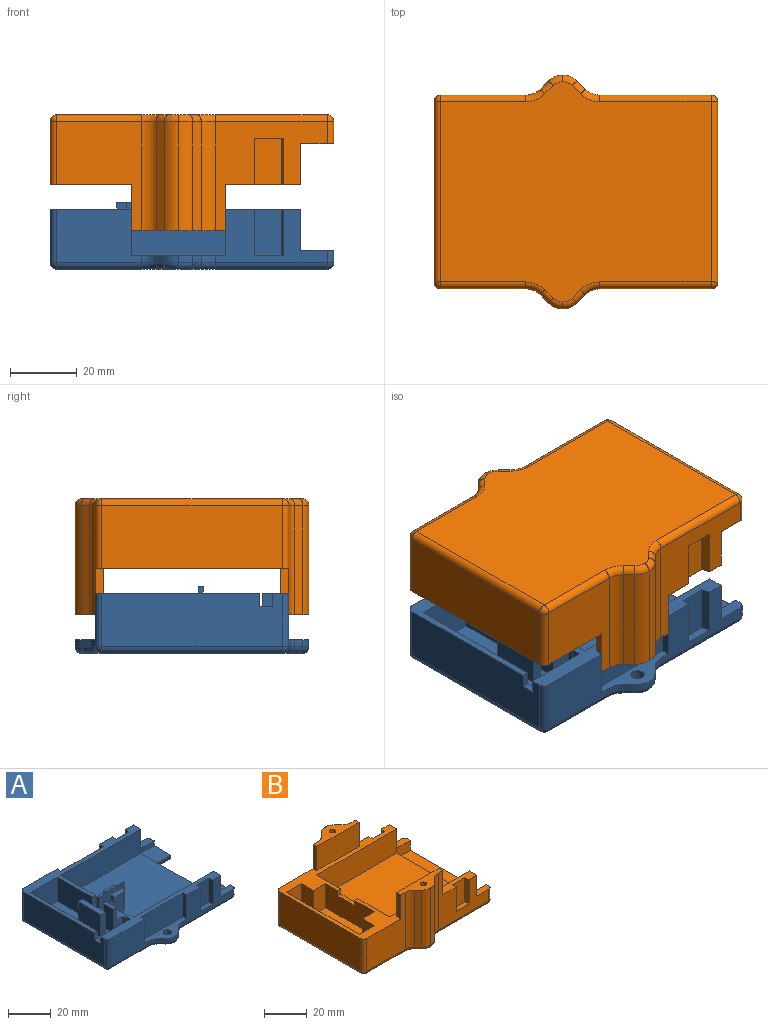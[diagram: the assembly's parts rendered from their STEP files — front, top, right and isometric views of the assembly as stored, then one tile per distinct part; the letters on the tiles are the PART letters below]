
ASSEMBLY  parts=2 mates=1
PART A: 140 faces, bbox 85x70x20 mm
  f0: plane 75x7.93mm, normal (0,0,1), area 280mm2, adj f3,f4,f9,f22,f23,f45,f46,f47
  f1: plane 48.25x13.88mm, normal (1,0,0), area 653.5mm2, adj f8,f51,f53,f54,f138,f139
  f2: plane 53x48.25mm, normal (0,0,1), area 2356.1mm2, adj f3,f7,f10,f11,f12,f13,f33,f34
  f3: plane 53x13.88mm, normal (0,1,0), area 694.8mm2, adj f0,f2,f9,f71,f72,f85
  f4: plane 33.51x15.88mm, normal (0,-1,0), area 272.1mm2, adj f0,f17,f19,f47,f48,f50,f83,f85
  f5: plane 12.88x3.65mm, normal (1,0,0), area 16.5mm2, adj f77,f78,f83,f84,f102,f103
  f6: plane 33.51x15.88mm, normal (0,1,0), area 272.1mm2, adj f8,f18,f20,f39,f41,f42,f82,f85
  f7: plane 53x13.88mm, normal (0,-1,0), area 735.4mm2, adj f2,f8,f13,f85
  f8: plane 75x49.13mm, normal (0,0,1), area 408mm2, adj f1,f6,f7,f13,f21,f22,f39,f40
  f9: plane 6.88x3.05mm, normal (1,0,0), area 21mm2, adj f0,f3,f72,f74
  f10: plane 13.88x11.3mm, normal (0,-1,0), area 89.3mm2, adj f2,f16,f32,f33,f63,f64,f71,f72
  f11: plane 13.88x0.8mm, normal (1,0,0), area 7.7mm2, adj f2,f16,f33,f34,f60,f64
  f12: plane 13.88x0.8mm, normal (1,0,0), area 7.7mm2, adj f2,f14,f36,f37,f65,f70
  f13: plane 23x13.88mm, normal (1,0,0), area 317.9mm2, adj f2,f7,f8,f38,f67,f70
  f14: plane 8.5x2.88mm, normal (0,0,1), area 20.8mm2, adj f12,f37,f38,f65,f66
  f15: plane 6.7x2mm, normal (0,0,1), area 13.4mm2, adj f32,f52,f59,f73
  f16: plane 8.5x2.88mm, normal (0,0,1), area 20.8mm2, adj f10,f11,f33,f60,f63
  f17: plane 8.67x2.5mm, normal (0,0,1), area 20.8mm2, adj f4,f48,f49,f50
  f18: plane 28x8.5mm, normal (0,0,1), area 123.4mm2, adj f6,f21,f28,f29,f30,f42,f43,f44
  f19: plane 28x8.5mm, normal (0,0,1), area 123.4mm2, adj f4,f23,f24,f25,f26,f45,f46,f47
  f20: plane 8.67x2.5mm, normal (0,0,1), area 20.8mm2, adj f6,f39,f40,f41
  f21: plane 25.51x15.88mm, normal (0,1,0), area 363.2mm2, adj f8,f18,f44,f94,f132,f137
  f22: plane 54x15.88mm, normal (-1,0,0), area 841.3mm2, adj f0,f8,f53,f127,f132,f133,f138,f139
  f23: plane 25.51x15.88mm, normal (0,-1,0), area 363.2mm2, adj f0,f19,f45,f87,f127,f128
  f24: plane 2.49x2.49mm, normal (-0.71,-0.71,0), area 7mm2, adj f19,f87,f88,f121,f123
  f25: plane 2.1x0.03mm, normal (0,-1,0), area 0.1mm2, adj f19,f88,f89,f117
  f26: plane 2.49x2.49mm, normal (0.71,-0.71,0), area 7mm2, adj f19,f89,f90,f110,f113
  f27: plane 12.88x3.65mm, normal (1,0,0), area 16.5mm2, adj f79,f80,f81,f82,f111,f112
  f28: plane 2.49x2.49mm, normal (0.71,0.71,0), area 7mm2, adj f18,f91,f92,f120,f122
  f29: plane 2.1x0.03mm, normal (0,1,0), area 0.1mm2, adj f18,f92,f93,f126
  f30: plane 2.49x2.49mm, normal (-0.71,0.71,0), area 7mm2, adj f18,f93,f94,f131,f134
  f31: plane 81x62.84mm, normal (0,0,-1), area 4097.4mm2, adj f57,f58,f103,f105,f106,f107,f108,f109
  f32: plane 6.88x6.7mm, normal (1,0,0), area 46.1mm2, adj f10,f15,f59,f72,f73
  f33: plane 13.88x2.7mm, normal (0.71,-0.71,0), area 53mm2, adj f2,f10,f11,f16
  f34: plane 15.88x14mm, normal (0,-1,0), area 111.8mm2, adj f2,f11,f35,f61,f64,f86
  f35: plane 15.88x0.5mm, normal (1,0,0), area 7.9mm2, adj f2,f34,f36,f86
  f36: plane 15.88x14mm, normal (0,1,0), area 111.7mm2, adj f2,f12,f35,f69,f70,f86
  f37: plane 13.88x2.7mm, normal (0.71,0.71,0), area 53mm2, adj f2,f12,f14,f38
  f38: plane 13.88x11.3mm, normal (0,1,0), area 129.9mm2, adj f2,f13,f14,f37,f66,f70,f101
  f39: plane 13.88x2.5mm, normal (-0.97,0.26,0), area 35.9mm2, adj f6,f8,f20,f40
  f40: plane 13.88x8mm, normal (0,1,0), area 111mm2, adj f8,f20,f39,f41
  f41: plane 13.88x2.5mm, normal (1,0,0), area 34.7mm2, adj f6,f8,f20,f40
  f42: plane 13.88x2.5mm, normal (-1,0,0), area 34.7mm2, adj f6,f8,f18,f43
  f43: plane 28x13.88mm, normal (0,1,0), area 388.5mm2, adj f8,f18,f42,f44
  f44: plane 13.88x2.5mm, normal (1,0,0), area 34.7mm2, adj f8,f18,f21,f43
  f45: plane 13.88x2.5mm, normal (1,0,0), area 34.7mm2, adj f0,f19,f23,f46
  f46: plane 28x13.88mm, normal (0,-1,0), area 388.5mm2, adj f0,f19,f45,f47
  f47: plane 13.88x2.5mm, normal (-1,0,0), area 34.7mm2, adj f0,f4,f19,f46
  f48: plane 13.88x2.5mm, normal (1,0,0), area 34.7mm2, adj f0,f4,f17,f49
  f49: plane 13.88x8mm, normal (0,-1,0), area 111mm2, adj f0,f17,f48,f50
  f50: plane 13.88x2.5mm, normal (-0.97,-0.26,0), area 35.9mm2, adj f0,f4,f17,f49
  f51: plane 18x13.88mm, normal (0,-1,0), area 249.8mm2, adj f1,f8,f52,f54
  f52: plane 48.25x15.88mm, normal (-1,0,0), area 536mm2, adj f0,f8,f15,f51,f53,f54,f59,f62
  f53: plane 20x13.88mm, normal (0,1,0), area 257.8mm2, adj f0,f1,f22,f52,f54,f139
  f54: plane 48.25x18mm, normal (0,0,1), area 823.5mm2, adj f1,f51,f52,f53,f95,f96,f97,f98
  f55: cylinder r=2mm len=4mm, axis (0,0,-1), area 31.4mm2, adj f18,f57
  f56: cylinder r=2mm len=4mm, axis (0,0,-1), area 31.4mm2, adj f19,f58
  f57: cone r=2mm half-angle=45deg, axis (0,0,-1), area 36.7mm2, adj f31,f55,f122,f124,f126,f129,f131
  f58: cone r=2mm half-angle=45deg, axis (0,0,-1), area 36.7mm2, adj f31,f56,f113,f115,f117,f119,f121
  f59: plane 5.38x2mm, normal (0,1,0), area 10.8mm2, adj f15,f32,f52,f64
  f60: plane 12x5.38mm, normal (0,1,0), area 48.3mm2, adj f11,f16,f63,f64,f100
  f61: plane 7.38x0.5mm, normal (1,0,0), area 3.7mm2, adj f34,f62,f64,f86
  f62: plane 7.38x3mm, normal (0,-1,0), area 22.1mm2, adj f52,f61,f64,f86
  f63: plane 2.88x1.88mm, normal (-1,0,0), area 5.4mm2, adj f10,f16,f60,f100
  f64: plane 16x3.5mm, normal (0,0,1), area 20mm2, adj f10,f11,f34,f52,f59,f60,f61,f62
  f65: plane 12x5.38mm, normal (0,-1,0), area 48.3mm2, adj f12,f14,f66,f70,f101
  f66: plane 2.88x1.88mm, normal (-1,0,0), area 5.4mm2, adj f14,f38,f65,f101
  f67: plane 5.38x2mm, normal (0,-1,0), area 10.8mm2, adj f8,f13,f52,f70
  f68: plane 7.38x3mm, normal (0,1,0), area 22.1mm2, adj f52,f69,f70,f86
  f69: plane 7.38x0.5mm, normal (1,0,0), area 3.7mm2, adj f36,f68,f70,f86
  f70: plane 16x3.73mm, normal (0,0,1), area 20.5mm2, adj f12,f13,f36,f38,f52,f65,f67,f68
  f71: plane 17.75x7mm, normal (1,0,0), area 124.3mm2, adj f2,f3,f10,f72
  f72: plane 17.75x5.8mm, normal (0,0,1), area 70.6mm2, adj f3,f9,f10,f32,f71,f73,f74,f75
  f73: plane 12.88x6.05mm, normal (0,-1,0), area 50mm2, adj f15,f32,f52,f72,f75,f76
  f74: plane 12.88x6.05mm, normal (0,1,0), area 50mm2, adj f0,f9,f52,f72,f75,f76
  f75: plane 8x6mm, normal (-1,0,0), area 48mm2, adj f72,f73,f74,f76
  f76: plane 8x6.05mm, normal (0,0,1), area 48.4mm2, adj f52,f73,f74,f75
  f77: plane 11.1x10mm, normal (0,0,1), area 111mm2, adj f5,f78,f84,f85
  f78: plane 10x0.9mm, normal (0,1,0), area 9mm2, adj f5,f77,f85,f105
  f79: plane 10x0.9mm, normal (0,-1,0), area 9mm2, adj f27,f80,f85,f109
  f80: plane 11.1x10mm, normal (0,0,1), area 111mm2, adj f27,f79,f81,f85
  f81: plane 10x2.75mm, normal (0,-1,0), area 27.5mm2, adj f27,f80,f82,f85
  f82: plane 10x3.78mm, normal (0,0,1), area 36.9mm2, adj f6,f27,f81,f85,f112
  f83: plane 10x3.78mm, normal (0,0,1), area 36.9mm2, adj f4,f5,f84,f85,f102
  f84: plane 10x2.75mm, normal (0,1,0), area 27.5mm2, adj f5,f77,f83,f85
  f85: plane 58x15.88mm, normal (1,0,0), area 203.7mm2, adj f0,f2,f3,f4,f6,f7,f8,f77
  f86: plane 17x1.5mm, normal (0,0,1), area 11.5mm2, adj f34,f35,f36,f52,f61,f62,f68,f69
  f87: cylinder r=6mm len=4.24mm, axis (0,0,1), area 9.4mm2, adj f19,f23,f24,f125
  f88: cylinder r=6mm len=4.24mm, axis (0,0,-1), area 9.7mm2, adj f19,f24,f25,f119
  f89: cylinder r=6mm len=4.24mm, axis (0,0,-1), area 9.7mm2, adj f19,f25,f26,f115
  f90: cylinder r=6mm len=4.24mm, axis (0,0,1), area 9.4mm2, adj f4,f19,f26,f108
  f91: cylinder r=6mm len=4.24mm, axis (0,0,1), area 9.4mm2, adj f6,f18,f28,f118
  f92: cylinder r=6mm len=4.24mm, axis (0,0,-1), area 9.7mm2, adj f18,f28,f29,f124
  f93: cylinder r=6mm len=4.24mm, axis (0,0,-1), area 9.7mm2, adj f18,f29,f30,f129
  f94: cylinder r=6mm len=4.24mm, axis (0,0,1), area 9.4mm2, adj f18,f21,f30,f136
  f95: plane 13x3mm, normal (0,1,0), area 39mm2, adj f54,f96,f98,f99
  f96: plane 15x13mm, normal (-1,0,0), area 195mm2, adj f54,f95,f97,f99
  f97: plane 13x3mm, normal (0,-1,0), area 39mm2, adj f54,f96,f98,f99
  f98: plane 15x13mm, normal (1,0,0), area 195mm2, adj f54,f95,f97,f99
  f99: plane 15x3mm, normal (0,0,1), area 45mm2, adj f95,f96,f97,f98
  f100: cylinder r=3.5mm len=3.5mm, axis (0,1,0), area 15.8mm2, adj f10,f60,f63,f64
  f101: cylinder r=3.5mm len=3.5mm, axis (0,1,0), area 15.8mm2, adj f38,f65,f66,f70
  f102: cylinder r=2mm len=3.65mm, axis (0,0,1), area 11.5mm2, adj f4,f5,f83,f104
  f103: cylinder r=2mm len=12.88mm, axis (0,1,0), area 38.2mm2, adj f5,f31,f104,f105
  f104: sphere r=2mm, area 6.3mm2, adj f102,f103,f106
  f105: cylinder r=2mm len=12mm, axis (1,0,0), area 31.4mm2, adj f31,f78,f103,f107
  f106: cylinder r=2mm len=33.51mm, axis (1,0,0), area 105.3mm2, adj f4,f31,f104,f108
  f107: cylinder r=2mm len=32.25mm, axis (0,1,0), area 93.3mm2, adj f31,f85,f105,f109
  f108: torus R=8mm, axis (0,0,1), area 16.6mm2, adj f31,f90,f106,f110
  f109: cylinder r=2mm len=12mm, axis (1,0,0), area 31.4mm2, adj f31,f79,f107,f111
  f110: cylinder r=2mm len=3.49mm, axis (0.71,0.71,0), area 9.2mm2, adj f26,f31,f108,f113
  f111: cylinder r=2mm len=12.88mm, axis (0,1,0), area 38.2mm2, adj f27,f31,f109,f114
  f112: cylinder r=2mm len=3.65mm, axis (0,0,-1), area 11.5mm2, adj f6,f27,f82,f114
  f113: bspline ~2.27x2.17mm, area 1.7mm2, adj f26,f58,f110,f115
  f114: sphere r=2mm, area 6.3mm2, adj f111,f112,f116
  f115: bspline ~6.14x3.55mm, area 11.5mm2, adj f58,f89,f113,f117
  f116: cylinder r=2mm len=33.51mm, axis (-1,0,0), area 105.3mm2, adj f6,f31,f114,f118
  f117: bspline ~1.91x1.4mm, area 0.1mm2, adj f25,f58,f115,f119
  f118: torus R=8mm, axis (0,0,1), area 16.6mm2, adj f31,f91,f116,f120
  f119: bspline ~5.92x3.89mm, area 11.5mm2, adj f58,f88,f117,f121
  f120: cylinder r=2mm len=3.49mm, axis (-0.71,0.71,0), area 9.2mm2, adj f28,f31,f118,f122
  f121: bspline ~2.27x2.17mm, area 1.7mm2, adj f24,f58,f119,f123
  f122: bspline ~2.27x2.17mm, area 1.7mm2, adj f28,f57,f120,f124
  f123: cylinder r=2mm len=3.49mm, axis (0.71,-0.71,0), area 9.2mm2, adj f24,f31,f121,f125
  f124: bspline ~5.92x3.89mm, area 11.5mm2, adj f57,f92,f122,f126
  f125: torus R=8mm, axis (0,0,1), area 16.6mm2, adj f31,f87,f123,f128
  f126: bspline ~1.91x1.4mm, area 0.1mm2, adj f29,f57,f124,f129
  f127: cylinder r=2mm len=15.88mm, axis (0,0,-1), area 49.9mm2, adj f0,f22,f23,f130
  f128: cylinder r=2mm len=25.51mm, axis (1,0,0), area 80.2mm2, adj f23,f31,f125,f130
  f129: bspline ~6.14x3.55mm, area 11.5mm2, adj f57,f93,f126,f131
  f130: sphere r=2mm, area 6.3mm2, adj f127,f128,f133
  f131: bspline ~2.27x2.17mm, area 1.7mm2, adj f30,f57,f129,f134
  f132: cylinder r=2mm len=15.88mm, axis (0,0,1), area 49.9mm2, adj f8,f21,f22,f135
  f133: cylinder r=2mm len=54mm, axis (0,-1,0), area 169.6mm2, adj f22,f31,f130,f135
  f134: cylinder r=2mm len=3.49mm, axis (-0.71,-0.71,0), area 9.2mm2, adj f30,f31,f131,f136
  f135: sphere r=2mm, area 6.3mm2, adj f132,f133,f137
  f136: torus R=8mm, axis (0,0,1), area 16.6mm2, adj f31,f94,f134,f137
  f137: cylinder r=2mm len=25.51mm, axis (-1,0,0), area 80.2mm2, adj f21,f31,f135,f136
  f138: plane 4x2mm, normal (0,-1,0), area 8mm2, adj f1,f8,f22,f139
  f139: plane 4x2mm, normal (0,0,1), area 8mm2, adj f1,f22,f53,f138
PART B: 92 faces, bbox 85x71x34.8 mm
  f0: plane 75x58mm, normal (0,0,1), area 846.4mm2, adj f1,f2,f4,f5,f6,f7,f12,f13
  f1: plane 48.25x13.88mm, normal (1,0,0), area 635.7mm2, adj f0,f3,f6,f7,f51,f52,f53
  f2: plane 32.25x13.88mm, normal (-1,0,0), area 413.7mm2, adj f0,f28,f29,f33,f51,f52,f53
  f3: plane 53x48.25mm, normal (0,0,1), area 2557.3mm2, adj f1,f6,f7,f48
  f4: plane 33.51x32.75mm, normal (0,-1,0), area 456.3mm2, adj f0,f8,f20,f22,f38,f41,f48,f50
  f5: plane 33.51x32.75mm, normal (0,1,0), area 456.3mm2, adj f0,f9,f23,f25,f36,f37,f48,f49
  f6: plane 53x13.88mm, normal (0,1,0), area 735.4mm2, adj f0,f1,f3,f48
  f7: plane 53x13.88mm, normal (0,-1,0), area 735.4mm2, adj f0,f1,f3,f48
  f8: plane 8.67x2.5mm, normal (0,0,1), area 20.8mm2, adj f4,f20,f21,f22
  f9: plane 8.67x2.5mm, normal (0,0,1), area 20.8mm2, adj f5,f23,f24,f25
  f10: plane 32.75x0.03mm, normal (0,1,0), area 1mm2, adj f37,f54,f61,f73
  f11: plane 32.75x2.49mm, normal (-0.71,0.71,0), area 115.1mm2, adj f37,f54,f55,f77
  f12: plane 32.75x25.51mm, normal (0,1,0), area 523.4mm2, adj f0,f34,f37,f55,f81,f82
  f13: plane 54x18.88mm, normal (-1,0,0), area 1019.3mm2, adj f0,f82,f86,f87
  f14: plane 32.75x25.51mm, normal (0,-1,0), area 523.4mm2, adj f0,f40,f41,f56,f87,f91
  f15: plane 32.75x2.49mm, normal (-0.71,-0.71,0), area 115.1mm2, adj f41,f56,f57,f88
  f16: plane 32.75x0.03mm, normal (0,-1,0), area 1mm2, adj f41,f57,f58,f83
  f17: plane 32.75x2.49mm, normal (0.71,-0.71,0), area 115.1mm2, adj f41,f58,f59,f78
  f18: plane 54x6.65mm, normal (1,0,0), area 74.1mm2, adj f46,f47,f49,f50,f63,f64,f69,f70
  f19: plane 32.75x2.49mm, normal (0.71,0.71,0), area 115.1mm2, adj f37,f60,f61,f68
  f20: plane 13.88x2.5mm, normal (1,0,0), area 34.7mm2, adj f0,f4,f8,f21
  f21: plane 13.88x8mm, normal (0,-1,0), area 111mm2, adj f0,f8,f20,f22
  f22: plane 13.88x2.5mm, normal (-0.97,-0.26,0), area 35.9mm2, adj f0,f4,f8,f21
  f23: plane 13.88x2.5mm, normal (-0.97,0.26,0), area 35.9mm2, adj f0,f5,f9,f24
  f24: plane 13.88x8mm, normal (0,1,0), area 111mm2, adj f0,f9,f23,f25
  f25: plane 13.88x2.5mm, normal (1,0,0), area 34.7mm2, adj f0,f5,f9,f24
  f26: plane 13.88x10mm, normal (0,-1,0), area 138.8mm2, adj f0,f27,f32,f33
  f27: plane 13.88x8mm, normal (-1,0,0), area 111mm2, adj f0,f26,f28,f33
  f28: plane 13.88x8mm, normal (0,-1,0), area 111mm2, adj f0,f2,f27,f33
  f29: plane 13.88x8mm, normal (0,1,0), area 111mm2, adj f0,f2,f30,f33
  f30: plane 13.88x8mm, normal (-1,0,0), area 111mm2, adj f0,f29,f31,f33
  f31: plane 13.88x10mm, normal (0,1,0), area 138.8mm2, adj f0,f30,f32,f33
  f32: plane 48.25x13.88mm, normal (1,0,0), area 669.5mm2, adj f0,f26,f31,f33
  f33: plane 48.25x18mm, normal (0,0,1), area 740.5mm2, adj f2,f26,f27,f28,f29,f30,f31,f32
  f34: plane 13.88x2.5mm, normal (-1,0,0), area 34.7mm2, adj f0,f12,f35,f37
  f35: plane 28x13.88mm, normal (0,-1,0), area 388.5mm2, adj f0,f34,f36,f37
  f36: plane 13.88x2.5mm, normal (1,0,0), area 34.7mm2, adj f0,f5,f35,f37
  f37: plane 28x8.5mm, normal (0,0,1), area 130.1mm2, adj f5,f10,f11,f12,f19,f34,f35,f36
  f38: plane 13.88x2.5mm, normal (1,0,0), area 34.7mm2, adj f0,f4,f39,f41
  f39: plane 28x13.88mm, normal (0,1,0), area 388.5mm2, adj f0,f38,f40,f41
  f40: plane 13.88x2.5mm, normal (-1,0,0), area 34.7mm2, adj f0,f14,f39,f41
  f41: plane 28x8.5mm, normal (0,0,1), area 130.1mm2, adj f4,f14,f15,f16,f17,f38,f39,f40
  f42: cylinder r=1.38mm len=10mm, axis (0,0,1), area 86.4mm2, adj f41,f43
  f43: plane 2.75x2.75mm, normal (0,0,1), area 5.9mm2, adj f42
  f44: cylinder r=1.38mm len=10mm, axis (0,0,1), area 86.4mm2, adj f37,f45
  f45: plane 2.75x2.75mm, normal (0,0,1), area 5.9mm2, adj f44
  f46: plane 10x5.65mm, normal (0,-1,0), area 56.5mm2, adj f18,f48,f49,f63
  f47: plane 10x5.65mm, normal (0,1,0), area 56.5mm2, adj f18,f48,f50,f63
  f48: plane 58x17.88mm, normal (1,0,0), area 324.6mm2, adj f0,f3,f4,f5,f6,f7,f46,f47
  f49: plane 10x3.78mm, normal (0,0,1), area 36.9mm2, adj f5,f18,f46,f48,f64
  f50: plane 10x3.78mm, normal (0,0,1), area 36.9mm2, adj f4,f18,f47,f48,f69
  f51: plane 3x2mm, normal (0,-1,0), area 6mm2, adj f0,f1,f2,f53
  f52: plane 3x2mm, normal (0,1,0), area 6mm2, adj f0,f1,f2,f53
  f53: plane 11.25x2mm, normal (0,0,1), area 22.5mm2, adj f1,f2,f51,f52
  f54: cylinder r=6mm len=32.75mm, axis (0,0,-1), area 154.3mm2, adj f10,f11,f37,f75
  f55: cylinder r=6mm len=32.75mm, axis (0,0,1), area 154.3mm2, adj f11,f12,f37,f79
  f56: cylinder r=6mm len=32.75mm, axis (0,0,1), area 154.3mm2, adj f14,f15,f41,f90
  f57: cylinder r=6mm len=32.75mm, axis (0,0,-1), area 154.3mm2, adj f15,f16,f41,f85
  f58: cylinder r=6mm len=32.75mm, axis (0,0,-1), area 154.3mm2, adj f16,f17,f41,f80
  f59: cylinder r=6mm len=32.75mm, axis (0,0,1), area 154.3mm2, adj f4,f17,f41,f76
  f60: cylinder r=6mm len=32.75mm, axis (0,0,1), area 154.3mm2, adj f5,f19,f37,f66
  f61: cylinder r=6mm len=32.75mm, axis (0,0,-1), area 154.3mm2, adj f10,f19,f37,f71
  f62: plane 81x66mm, normal (0,0,-1), area 4490.2mm2, adj f65,f66,f68,f70,f71,f73,f74,f75
  f63: plane 50.45x10mm, normal (0,0,1), area 504.5mm2, adj f18,f46,f47,f48
  f64: cylinder r=2mm len=6.65mm, axis (0,0,1), area 20.9mm2, adj f5,f18,f49,f67
  f65: cylinder r=2mm len=33.51mm, axis (1,0,0), area 105.3mm2, adj f5,f62,f66,f67
  f66: torus R=8mm, axis (0,0,-1), area 16.6mm2, adj f60,f62,f65,f68
  f67: sphere r=2mm, area 6.3mm2, adj f64,f65,f70
  f68: cylinder r=2mm len=3.9mm, axis (0.71,-0.71,0), area 11mm2, adj f19,f62,f66,f71
  f69: cylinder r=2mm len=6.65mm, axis (0,0,-1), area 20.9mm2, adj f4,f18,f50,f72
  f70: cylinder r=2mm len=54mm, axis (0,1,0), area 169.6mm2, adj f18,f62,f67,f72
  f71: torus R=4mm, axis (0,0,-1), area 13mm2, adj f61,f62,f68,f73
  f72: sphere r=2mm, area 6.3mm2, adj f69,f70,f74
  f73: cylinder r=2mm len=2mm, axis (1,0,0), area 0.1mm2, adj f10,f62,f71,f75
  f74: cylinder r=2mm len=33.51mm, axis (-1,0,0), area 105.3mm2, adj f4,f62,f72,f76
  f75: torus R=4mm, axis (0,0,-1), area 13mm2, adj f54,f62,f73,f77
  f76: torus R=8mm, axis (0,0,-1), area 16.6mm2, adj f59,f62,f74,f78
  f77: cylinder r=2mm len=3.9mm, axis (0.71,0.71,0), area 11mm2, adj f11,f62,f75,f79
  f78: cylinder r=2mm len=3.9mm, axis (-0.71,-0.71,0), area 11mm2, adj f17,f62,f76,f80
  f79: torus R=8mm, axis (0,0,-1), area 16.6mm2, adj f55,f62,f77,f81
  f80: torus R=4mm, axis (0,0,-1), area 13mm2, adj f58,f62,f78,f83
  f81: cylinder r=2mm len=25.51mm, axis (1,0,0), area 80.2mm2, adj f12,f62,f79,f84
  f82: cylinder r=2mm len=18.88mm, axis (0,0,-1), area 59.3mm2, adj f0,f12,f13,f84
  f83: cylinder r=2mm len=2mm, axis (-1,0,0), area 0.1mm2, adj f16,f62,f80,f85
  f84: sphere r=2mm, area 6.3mm2, adj f81,f82,f86
  f85: torus R=4mm, axis (0,0,-1), area 13mm2, adj f57,f62,f83,f88
  f86: cylinder r=2mm len=54mm, axis (0,1,0), area 169.6mm2, adj f13,f62,f84,f89
  f87: cylinder r=2mm len=18.88mm, axis (0,0,1), area 59.3mm2, adj f0,f13,f14,f89
  f88: cylinder r=2mm len=3.9mm, axis (-0.71,0.71,0), area 11mm2, adj f15,f62,f85,f90
  f89: sphere r=2mm, area 6.3mm2, adj f86,f87,f91
  f90: torus R=8mm, axis (0,0,-1), area 16.6mm2, adj f56,f62,f88,f91
  f91: cylinder r=2mm len=25.51mm, axis (-1,0,0), area 80.2mm2, adj f14,f62,f89,f90
PLACE A t=(8.56,-1.22,8.23)mm
PLACE B rot(axis=(1,0,0),180deg) t=(8.56,-1.22,51.48)mm
MATE cylindrical B.f44 <-> A.f56  axis (0,0,-1) through (-37.94,7.66,19.73)mm
